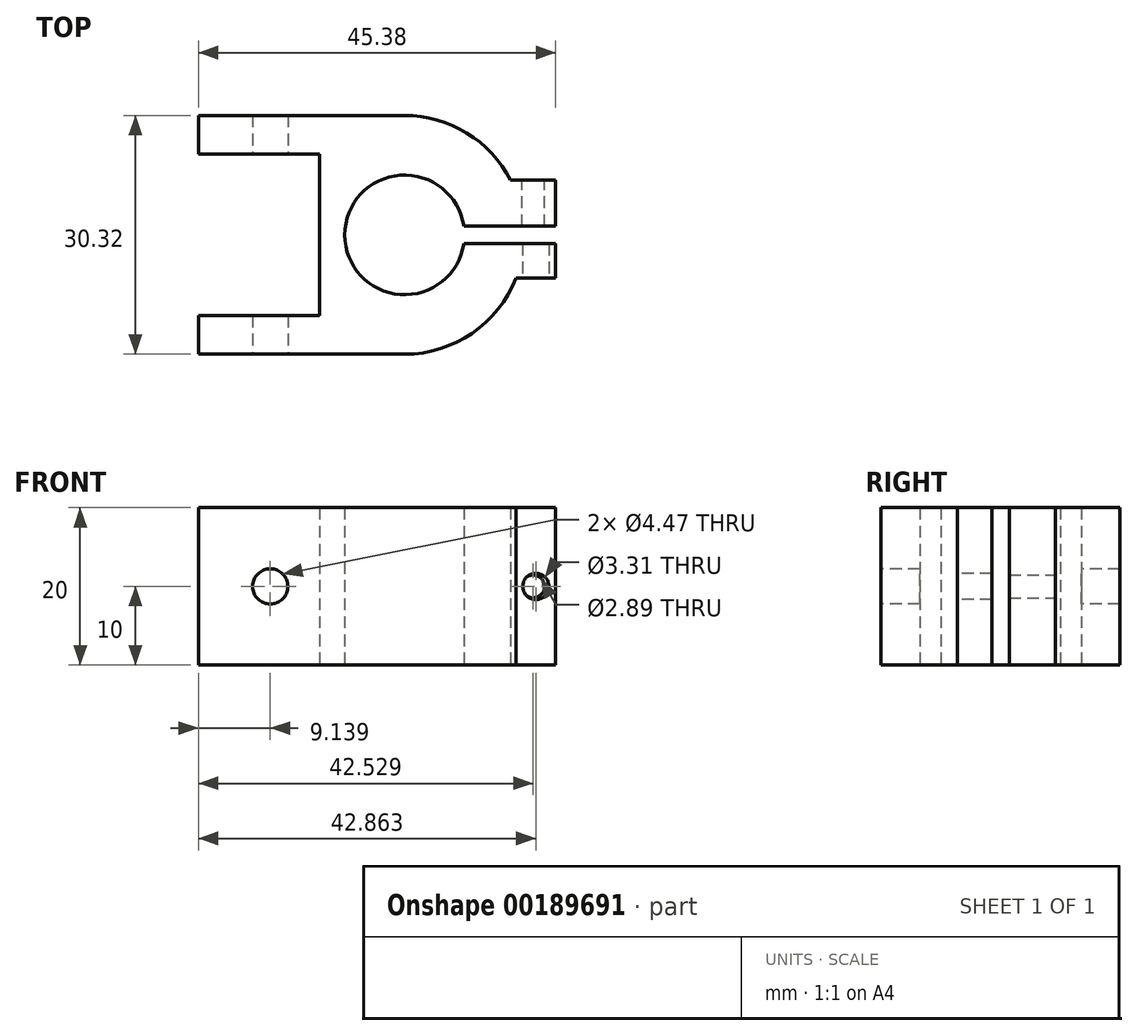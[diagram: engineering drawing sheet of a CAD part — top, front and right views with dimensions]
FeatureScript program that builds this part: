
annotation { "Feature Type Name" : "Feature", "Feature Type Description" : "" }
export const myFeature = defineFeature(function(context is Context, id is Id, definition is map)
    precondition{}
    {
        {
            var Q0;
            Q0=qCreatedBy(makeId("Top.planeOp"),FACE);
            var sketch = newSketch(context, id + "F0", { "sketchPlane" : qUnion([Q0])});
            skArc(sketch, "E0", {"start": v(7.52, 1.1) * mm, "mid": v(-7.6, 0) * mm, "end": v(7.52, -1.1) * mm});
            skArc(sketch, "E1", {"start": v(0, -15.16) * mm, "mid": v(8.58, -12.5) * mm, "end": v(14.15, -5.46) * mm});
            skLineSegment(sketch, "E2.bottom", {"start": v(-48.25, 10.25) * mm, "end": v(-10.79, 10.25) * mm, "construction": true});
            skLineSegment(sketch, "E2.top", {"start": v(-48.25, -10.25) * mm, "end": v(-10.79, -10.25) * mm, "construction": true});
            skLineSegment(sketch, "E2.left", {"start": v(-48.25, 10.25) * mm, "end": v(-48.25, -10.25) * mm, "construction": true});
            skLineSegment(sketch, "E2.right", {"start": v(-10.79, 10.25) * mm, "end": v(-10.79, -10.25) * mm, "construction": true});
            skLineSegment(sketch, "E3", {"start": v(0, 0) * mm, "end": v(-10.79, 0) * mm, "construction": true});
            skLineSegment(sketch, "E4", {"start": v(0, 15.16) * mm, "end": v(-26.2, 15.16) * mm});
            skLineSegment(sketch, "E5", {"start": v(-26.2, 15.16) * mm, "end": v(-26.2, 10.25) * mm});
            skPoint(sketch, "E5.endSnap0", {"position": v(-29.52, 10.25) * mm});
            skLineSegment(sketch, "E6", {"start": v(-26.2, 10.25) * mm, "end": v(-10.79, 10.25) * mm});
            skLineSegment(sketch, "E7", {"start": v(-10.79, 10.25) * mm, "end": v(-10.79, -10.25) * mm});
            skLineSegment(sketch, "E8", {"start": v(-10.79, -10.25) * mm, "end": v(-26.2, -10.25) * mm});
            skLineSegment(sketch, "E9", {"start": v(-26.2, -10.25) * mm, "end": v(-26.2, -15.16) * mm});
            skLineSegment(sketch, "E10", {"start": v(-26.2, -15.16) * mm, "end": v(0, -15.16) * mm});
            skLineSegment(sketch, "E11", {"start": v(13.48, 6.94) * mm, "end": v(19.18, 6.94) * mm});
            skLineSegment(sketch, "E12", {"start": v(19.18, 6.94) * mm, "end": v(19.18, 1.1) * mm});
            skLineSegment(sketch, "E13", {"start": v(19.18, 1.1) * mm, "end": v(7.52, 1.1) * mm});
            skLineSegment(sketch, "E14", {"start": v(7.52, -1.1) * mm, "end": v(19.18, -1.1) * mm});
            skLineSegment(sketch, "E15", {"start": v(19.18, -1.1) * mm, "end": v(19.18, -5.46) * mm});
            skLineSegment(sketch, "E16", {"start": v(19.18, -5.46) * mm, "end": v(14.15, -5.46) * mm});
            skArc(sketch, "E17.trimOffspring", {"start": v(13.48, 6.94) * mm, "mid": v(7.9, 12.95) * mm, "end": v(0, 15.16) * mm});
            skSolve(sketch);
        }
        {
            var Q0;
            Q0=makeQuery(id+"F0.imprint","IMPRINT",FACE,{"disambiguationData":[TD([[makeQuery(id+"F0.imprint","IMPRINT",EDGE,{"derivedFrom":sQuery(id+"F0.wireOp",EDGE,"E0")}),-1.0]])]});
            extrude(context, id + "F1", {"entities" : qUnion([Q0]), "depth" : 20 * mm});
        }
        {
            var Q0;
            Q0=makeQuery(id+"F1.opExtrude","SWEPT_FACE",FACE,{"disambiguationData":[OSD([sQuery(id+"F0.wireOp",EDGE,"E16")])]});
            var sketch = newSketch(context, id + "F2", { "sketchPlane" : qUnion([Q0])});
            skCircle(sketch, "E18", {"center": v(16.66, 10) * mm, "radius": 1.66 * mm});
            skPoint(sketch, "E18.centerSnap0", {"position": v(16.66, 20) * mm});
            skPoint(sketch, "E18.centerSnap1", {"position": v(19.18, 10) * mm});
            skSolve(sketch);
        }
        {
            var Q0;
            Q0=qSketchRegion(id+"F2",true);
            extrude(context, id + "F3", {"entities" : qUnion([Q0]), "operationType" : NewBodyOperationType.REMOVE, "endBound" : BoundingType.UP_TO_NEXT, "oppositeDirection" : true, "depth" : 25 * mm});
        }
        {
            var Q0;
            Q0=makeQuery(id+"F1.opExtrude","SWEPT_FACE",FACE,{"disambiguationData":[OSD([sQuery(id+"F0.wireOp",EDGE,"E11")])]});
            var sketch = newSketch(context, id + "F4", { "sketchPlane" : qUnion([Q0])});
            skCircle(sketch, "E19", {"center": v(-16.33, 10) * mm, "radius": 1.45 * mm});
            skPoint(sketch, "E19.centerSnap0", {"position": v(-19.18, 10) * mm});
            skPoint(sketch, "E19.centerSnap1", {"position": v(-16.33, 20) * mm});
            skSolve(sketch);
        }
        {
            var Q0;
            Q0=qSketchRegion(id+"F4",true);
            extrude(context, id + "F5", {"entities" : qUnion([Q0]), "operationType" : NewBodyOperationType.REMOVE, "endBound" : BoundingType.UP_TO_NEXT, "oppositeDirection" : true, "depth" : 25 * mm});
        }
        {
            var Q0;
            Q0=makeQuery(id+"F1.opExtrude","SWEPT_FACE",FACE,{"disambiguationData":[OSD([sQuery(id+"F0.wireOp",EDGE,"E10")])]});
            var sketch = newSketch(context, id + "F6", { "sketchPlane" : qUnion([Q0])});
            skCircle(sketch, "E20", {"center": v(-17.06, 10) * mm, "radius": 2.24 * mm});
            skPoint(sketch, "E20.centerSnap0", {"position": v(-26.2, 10) * mm});
            skSolve(sketch);
        }
        {
            var Q0;
            Q0=qSketchRegion(id+"F6",true);
            extrude(context, id + "F7", {"entities" : qUnion([Q0]), "operationType" : NewBodyOperationType.REMOVE, "endBound" : BoundingType.THROUGH_ALL, "oppositeDirection" : true, "depth" : 25 * mm});
        }
    });
